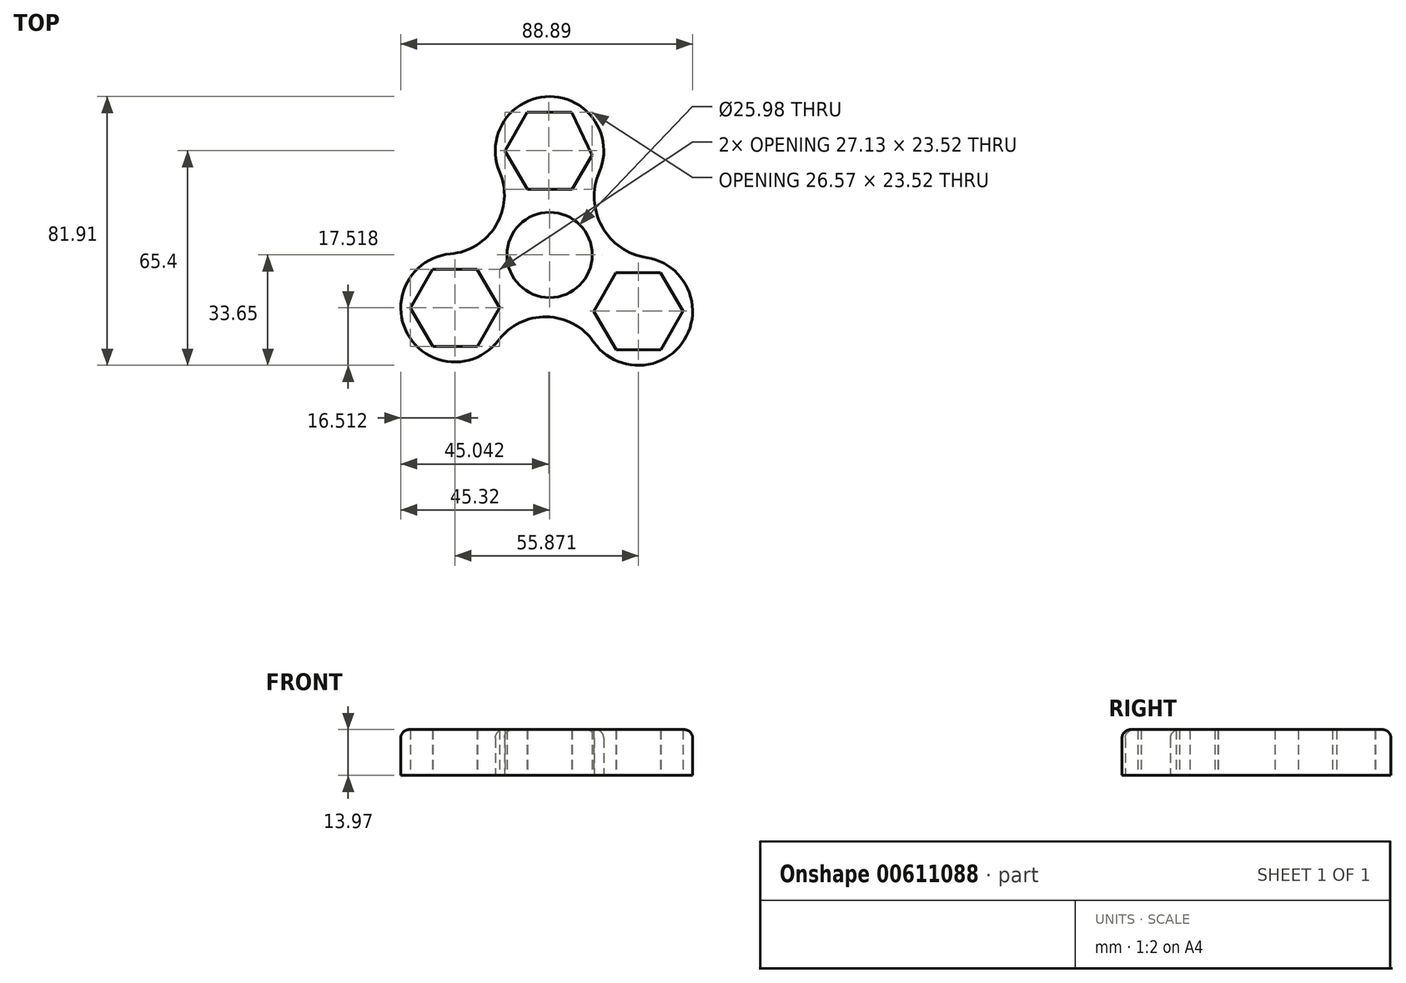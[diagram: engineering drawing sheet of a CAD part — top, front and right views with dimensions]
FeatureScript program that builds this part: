
annotation { "Feature Type Name" : "Feature", "Feature Type Description" : "" }
export const myFeature = defineFeature(function(context is Context, id is Id, definition is map)
    precondition{}
    {
        {
            var Q0;
            Q0=qCreatedBy(makeId("Top.planeOp"),FACE);
            var sketch = newSketch(context, id + "F0", { "sketchPlane" : qUnion([Q0])});
            skCircle(sketch, "E0", {"center": v(0, 0) * mm, "radius": 13 * mm});
            skLineSegment(sketch, "E1.0", {"start": v(-6.76, 19.99) * mm, "end": v(-13.56, 31.72) * mm});
            skLineSegment(sketch, "E1.1", {"start": v(-13.56, 31.72) * mm, "end": v(-6.8, 43.48) * mm});
            skLineSegment(sketch, "E1.2", {"start": v(-6.8, 43.48) * mm, "end": v(6.76, 43.51) * mm});
            skLineSegment(sketch, "E1.3", {"start": v(6.76, 43.51) * mm, "end": v(13, 30.4) * mm});
            skLineSegment(sketch, "E1.4", {"start": v(13, 30.4) * mm, "end": v(6.8, 20.02) * mm});
            skLineSegment(sketch, "E1.5", {"start": v(6.8, 20.02) * mm, "end": v(-6.76, 19.99) * mm});
            skLineSegment(sketch, "E2.0", {"start": v(-35.56, -27.9) * mm, "end": v(-42.37, -16.16) * mm});
            skLineSegment(sketch, "E2.1", {"start": v(-42.37, -16.16) * mm, "end": v(-35.61, -4.4) * mm});
            skLineSegment(sketch, "E2.2", {"start": v(-35.61, -4.4) * mm, "end": v(-22.05, -4.37) * mm});
            skLineSegment(sketch, "E2.3", {"start": v(-22.05, -4.37) * mm, "end": v(-15.24, -16.1) * mm});
            skLineSegment(sketch, "E2.4", {"start": v(-15.24, -16.1) * mm, "end": v(-22, -27.86) * mm});
            skLineSegment(sketch, "E2.5", {"start": v(-22, -27.86) * mm, "end": v(-35.56, -27.9) * mm});
            skLineSegment(sketch, "E3.0", {"start": v(20.3, -28.9) * mm, "end": v(13.5, -17.17) * mm});
            skLineSegment(sketch, "E3.1", {"start": v(13.5, -17.17) * mm, "end": v(20.26, -5.4) * mm});
            skLineSegment(sketch, "E3.2", {"start": v(20.26, -5.4) * mm, "end": v(33.82, -5.38) * mm});
            skLineSegment(sketch, "E3.3", {"start": v(33.82, -5.38) * mm, "end": v(40.63, -17.11) * mm});
            skLineSegment(sketch, "E3.4", {"start": v(40.63, -17.11) * mm, "end": v(33.87, -28.87) * mm});
            skLineSegment(sketch, "E3.5", {"start": v(33.87, -28.87) * mm, "end": v(20.3, -28.9) * mm});
            skArc(sketch, "E4", {"start": v(-30.2, 0.32) * mm, "mid": v(-16.33, 8.97) * mm, "end": v(-15.2, 25.28) * mm});
            skArc(sketch, "E5", {"start": v(13.52, -26.58) * mm, "mid": v(-0.91, -18.88) * mm, "end": v(-15.61, -26.05) * mm});
            skArc(sketch, "E6", {"start": v(15.16, 25.21) * mm, "mid": v(15.98, 8.66) * mm, "end": v(29.57, -0.82) * mm});
            skPoint(sketch, "E6.startSnap0", {"position": v(9.9, 25.21) * mm});
            skArc(sketch, "E7", {"start": v(-30.2, 0.32) * mm, "mid": v(-43.25, -24.13) * mm, "end": v(-15.61, -26.05) * mm});
            skArc(sketch, "E8", {"start": v(13.52, -26.58) * mm, "mid": v(41.07, -25.87) * mm, "end": v(29.57, -0.82) * mm});
            skArc(sketch, "E9", {"start": v(15.16, 25.21) * mm, "mid": v(0.04, 48.26) * mm, "end": v(-15.2, 25.28) * mm});
            skSolve(sketch);
        }
        {
            var Q0;
            Q0 = qSketchRegion(id + "F0", true);
            extrude(context, id + "F1", {"entities" : qUnion([Q0]), "depth" : 13.97 * mm, "offsetDistance" : 25.4 * mm});
        }
        {
            var Q0;
            Q0=makeQuery(id+"F1.opExtrude","CAP_EDGE",EDGE,{"disambiguationData":[OSD([sQuery(id+"F0.wireOp",EDGE,"E5")])],"isStart":false});
            var Q1;
            Q1=makeQuery(id+"F1.opExtrude","CAP_EDGE",EDGE,{"disambiguationData":[OSD([sQuery(id+"F0.wireOp",EDGE,"E7")])],"isStart":false});
            var Q2;
            Q2=makeQuery(id+"F1.opExtrude","CAP_EDGE",EDGE,{"disambiguationData":[OSD([sQuery(id+"F0.wireOp",EDGE,"E4")])],"isStart":false});
            var Q3;
            Q3=makeQuery(id+"F1.opExtrude","CAP_EDGE",EDGE,{"disambiguationData":[OSD([sQuery(id+"F0.wireOp",EDGE,"E9")])],"isStart":false});
            var Q4;
            Q4=makeQuery(id+"F1.opExtrude","CAP_EDGE",EDGE,{"disambiguationData":[OSD([sQuery(id+"F0.wireOp",EDGE,"E6")])],"isStart":false});
            var Q5;
            Q5=makeQuery(id+"F1.opExtrude","CAP_EDGE",EDGE,{"disambiguationData":[OSD([sQuery(id+"F0.wireOp",EDGE,"E8")])],"isStart":false});
            fillet(context, id + "F2", {"entities" : qUnion([Q0, Q1, Q2, Q3, Q4, Q5]), "radius" : 2.54 * mm, "tangentPropagation" : true, "allowEdgeOverflow" : false});
        }
    });
